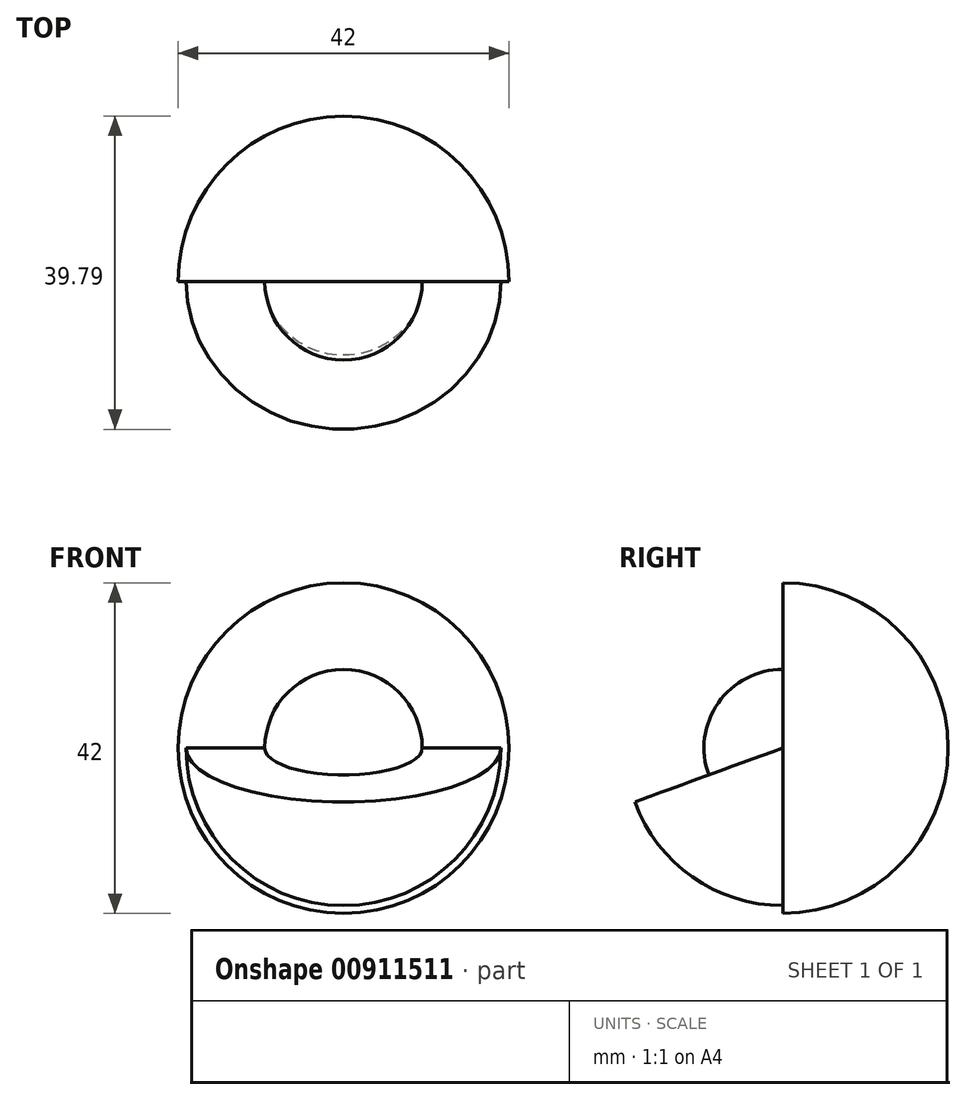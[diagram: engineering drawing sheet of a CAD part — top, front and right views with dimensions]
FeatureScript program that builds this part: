
annotation { "Feature Type Name" : "Feature", "Feature Type Description" : "" }
export const myFeature = defineFeature(function(context is Context, id is Id, definition is map)
    precondition{}
    {
        {
            var Q0;
            Q0=qCreatedBy(makeId("Front.planeOp"),FACE);
            var sketch = newSketch(context, id + "F0", { "sketchPlane" : qUnion([Q0])});
            skArc(sketch, "E0", {"start": v(0, -21) * mm, "mid": v(21, 0) * mm, "end": v(0, 21) * mm});
            skArc(sketch, "E1", {"start": v(0, -20) * mm, "mid": v(20, 0) * mm, "end": v(0, 20) * mm});
            skArc(sketch, "E2", {"start": v(0, -10) * mm, "mid": v(10, 0) * mm, "end": v(0, 10) * mm});
            skLineSegment(sketch, "E3", {"start": v(0, 21) * mm, "end": v(0, -21) * mm});
            skLineSegment(sketch, "E4", {"start": v(0, -21) * mm, "end": v(0, 21) * mm});
            skSolve(sketch);
        }
        {
            var Q0;
            {var subQ0=sQuery(id+"F0.wireOp",EDGE,"E0");Q0=makeQuery(id+"F0.imprint","IMPRINT",FACE,{"disambiguationData":[TD([[makeQuery(id+"F0.imprint","IMPRINT",EDGE,{"derivedFrom":subQ0}),1.0]])]});}
            var Q1;
            Q1=sQuery(id+"F0.wireOp",EDGE,"E3");
            revolve(context, id + "F1", {"surfaceOperationType" : NewSurfaceOperationType.NEW, "entities" : qUnion([Q0]), "axis" : qUnion([Q1]), "revolveType" : RevolveType.ONE_DIRECTION, "oppositeDirection" : true, "angle" : 180 * degree});
        }
        {
            var Q0;
            Q0=qCreatedBy(makeId("Front.planeOp"),FACE);
            var sketch = newSketch(context, id + "F2", { "sketchPlane" : qUnion([Q0])});
            skArc(sketch, "E5", {"start": v(20, 0) * mm, "mid": v(0, 20) * mm, "end": v(-20, 0) * mm});
            skArc(sketch, "E6", {"start": v(10, 0) * mm, "mid": v(0, 10) * mm, "end": v(-10, 0) * mm});
            skLineSegment(sketch, "E7", {"start": v(20, 0) * mm, "end": v(-20, 0) * mm});
            skLineSegment(sketch, "E8", {"start": v(-20, 0) * mm, "end": v(21, 0) * mm});
            skSolve(sketch);
        }
        {
            var Q0;
            {var subQ0=sQuery(id+"F2.wireOp",EDGE,"E5");Q0=makeQuery(id+"F2.imprint","IMPRINT",FACE,{"disambiguationData":[TD([[makeQuery(id+"F2.imprint","IMPRINT",EDGE,{"derivedFrom":subQ0}),1.0]])]});}
            var Q1;
            Q1=sQuery(id+"F2.wireOp",EDGE,"E7");
            revolve(context, id + "F3", {"operationType" : NewBodyOperationType.ADD, "surfaceOperationType" : NewSurfaceOperationType.NEW, "entities" : qUnion([Q0]), "axis" : qUnion([Q1]), "revolveType" : RevolveType.ONE_DIRECTION, "angle" : 250 * degree});
        }
        {
            var Q0;
            Q0=qCreatedBy(makeId("Front.planeOp"),FACE);
            var sketch = newSketch(context, id + "F4", { "sketchPlane" : qUnion([Q0])});
            skArc(sketch, "E9", {"start": v(-10, 0) * mm, "mid": v(0, -10) * mm, "end": v(10, 0) * mm});
            skLineSegment(sketch, "E10", {"start": v(-10, 0) * mm, "end": v(10, 0) * mm});
            skSolve(sketch);
        }
        {
            var Q0;
            Q0=makeQuery(id+"F4.imprint","IMPRINT",FACE,{"disambiguationData":[TD([[makeQuery(id+"F4.imprint","IMPRINT",EDGE,{"derivedFrom":sQuery(id+"F4.wireOp",EDGE,"E9")}),1.0]])]});
            var Q1;
            Q1=sQuery(id+"F4.wireOp",EDGE,"E10");
            revolve(context, id + "F5", {"operationType" : NewBodyOperationType.ADD, "surfaceOperationType" : NewSurfaceOperationType.NEW, "entities" : qUnion([Q0]), "axis" : qUnion([Q1]), "revolveType" : RevolveType.FULL});
        }
    });
